# Revit family: Qf_Summit_SEIH4636CV4_36 inches Wide Island Hood
name_source: partatom
category: Specialty Equipment
units: mm (PartAtom-declared; Revit-internal decimal feet)

## family parameters
Always vertical = Yes
Cut with Voids When Loaded = No
Part Type = Normal
Room Calculation Point = No
Round Connector Dimension = Use Diameter
Shared = No
Work Plane-Based = No

## types (1)
- Qf_Summit_SEIH4636CV4_36 inches Wide Island Hood
    Default Elevation = 0"
    Depth = 23 5/8"
    Description = 36" Wide Island Hood
    Exhaust RI Height = 0"
    Exhaust Static Press = 0.00 in-wg
    Exhaust Vent Depth = 15"
    Exhaust Vent Diameter = 0"
    Exhaust Vent Width = 9"
    Exhaust Volume = 200 CFM
    Foodservice Equipment Identifier = Yes
    Height = 33"
    Identify Quantity as Lot = Yes
    Length = 35 5/8"
    MU Air Volume = 0 CFM
    Manufacturer = Summit
    Model = SEIH4636CV4
    Weight in Pounds = 51

## geometry (parser evidence)
native form markers: Sweep x2
no freeform markers — native parametric forms only
